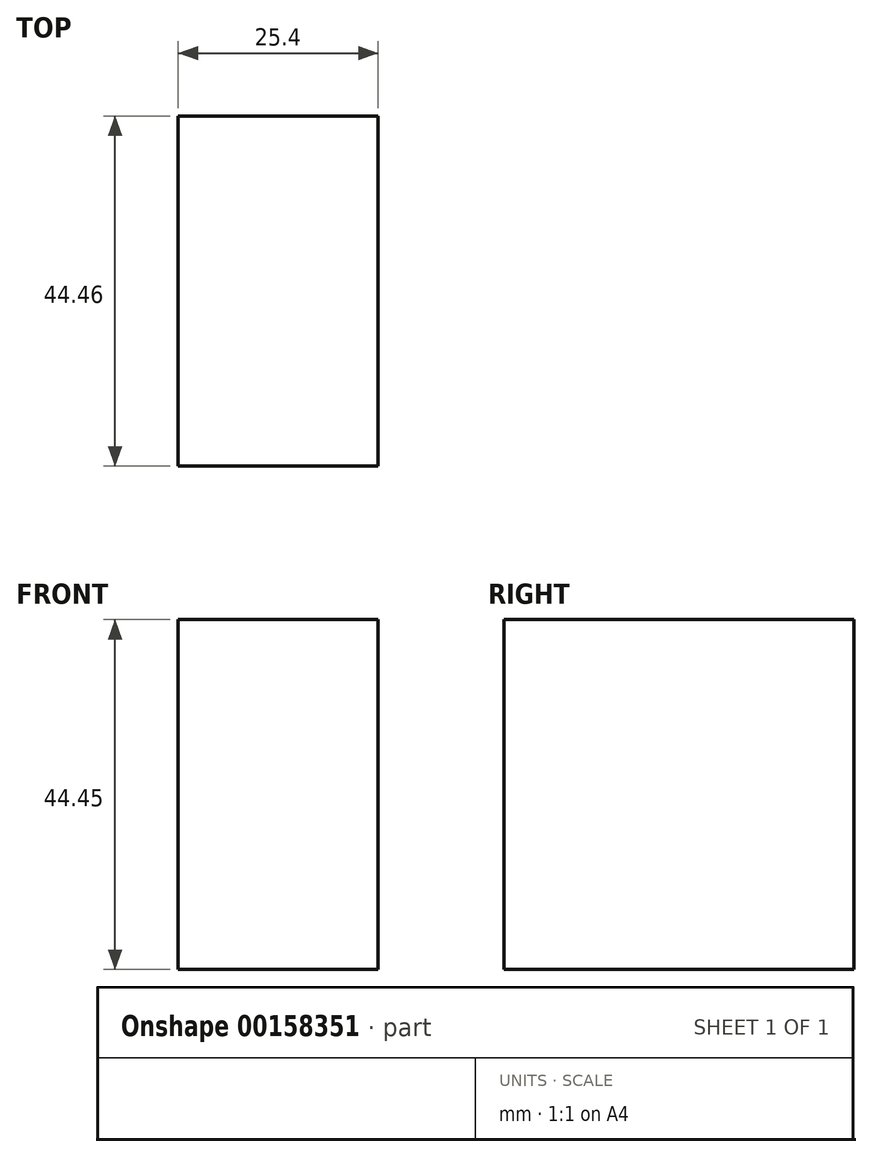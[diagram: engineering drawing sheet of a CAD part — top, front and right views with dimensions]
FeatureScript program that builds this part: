
annotation { "Feature Type Name" : "Feature", "Feature Type Description" : "" }
export const myFeature = defineFeature(function(context is Context, id is Id, definition is map)
    precondition{}
    {
        {
            var Q0;
            Q0=qCreatedBy(makeId("Front.planeOp"),FACE);
            var sketch = newSketch(context, id + "F0", { "sketchPlane" : qUnion([Q0])});
            skLineSegment(sketch, "E0.bottom", {"start": v(-59.53, 60.44) * mm, "end": v(-34.13, 60.44) * mm});
            skLineSegment(sketch, "E0.top", {"start": v(-59.53, 16) * mm, "end": v(-34.13, 16) * mm});
            skLineSegment(sketch, "E0.left", {"start": v(-59.53, 60.44) * mm, "end": v(-59.53, 16) * mm});
            skLineSegment(sketch, "E0.right", {"start": v(-34.13, 60.44) * mm, "end": v(-34.13, 16) * mm});
            skSolve(sketch);
        }
        {
            var Q0;
            Q0=makeQuery(id+"F0.imprint","IMPRINT",FACE,{"disambiguationData":[TD([[makeQuery(id+"F0.imprint","IMPRINT",EDGE,{"derivedFrom":sQuery(id+"F0.wireOp",EDGE,"E0.bottom")}),-1.0]])]});
            extrude(context, id + "F1", {"entities" : qUnion([Q0]), "endBound" : BoundingType.SYMMETRIC, "depth" : 44.45 * mm});
        }
    });
